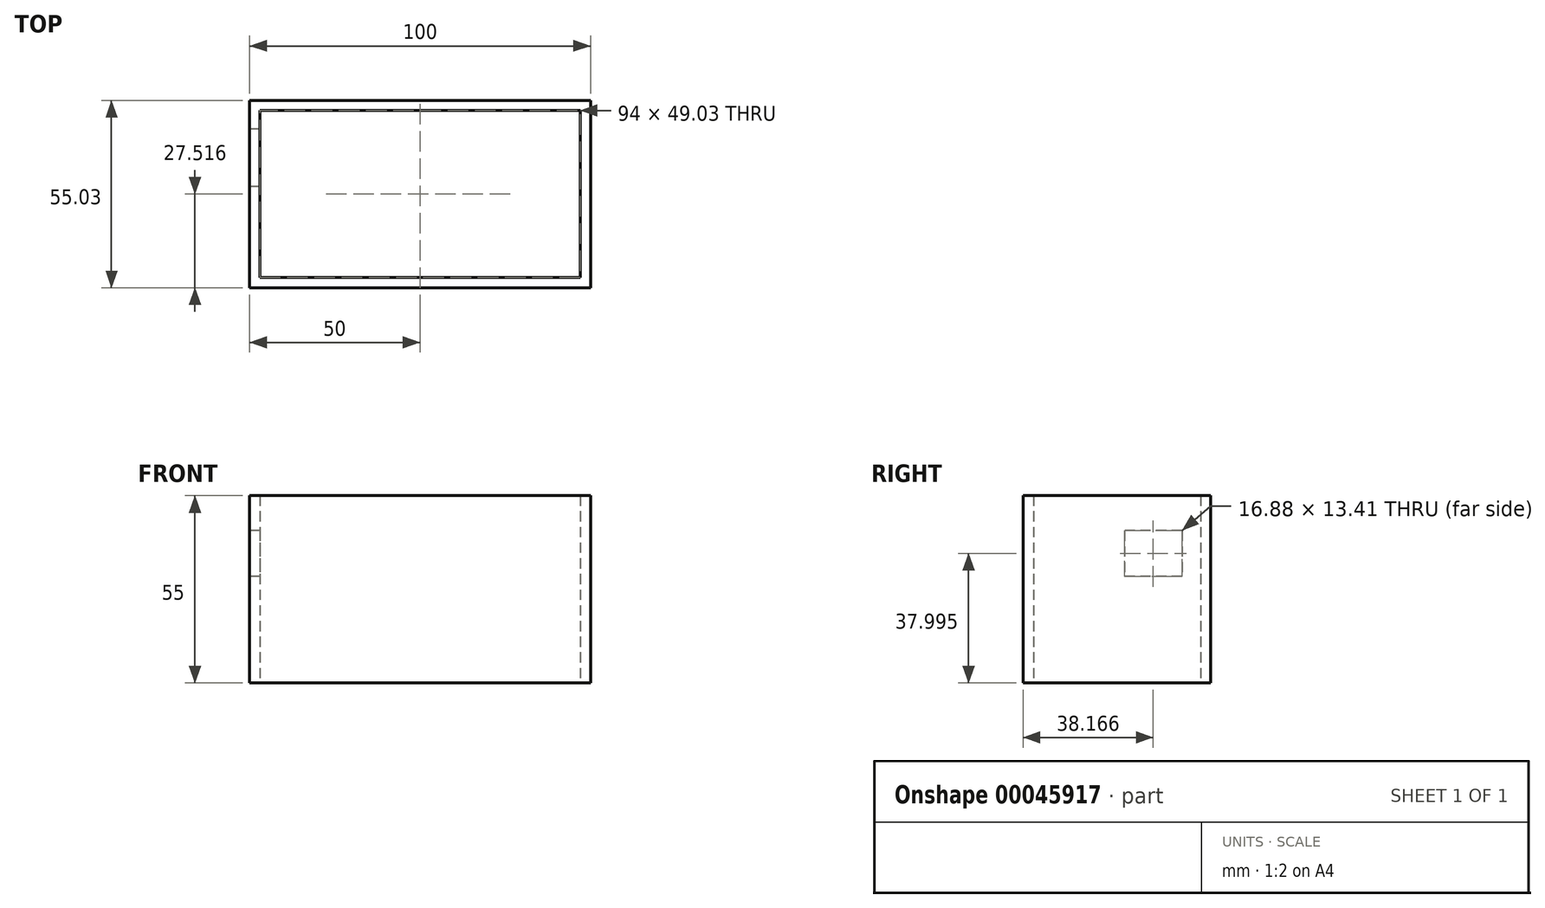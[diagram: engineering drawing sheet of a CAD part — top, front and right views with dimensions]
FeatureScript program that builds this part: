
annotation { "Feature Type Name" : "Feature", "Feature Type Description" : "" }
export const myFeature = defineFeature(function(context is Context, id is Id, definition is map)
    precondition{}
    {
        {
            var Q0;
            Q0=qCreatedBy(makeId("Top.planeOp"),FACE);
            var sketch = newSketch(context, id + "F0", { "sketchPlane" : qUnion([Q0])});
            skLineSegment(sketch, "E0.bottom", {"start": v(3, 0) * mm, "end": v(-97, 0) * mm});
            skLineSegment(sketch, "E0.top", {"start": v(3, 55.03) * mm, "end": v(-97, 55.03) * mm});
            skLineSegment(sketch, "E0.left", {"start": v(3, 0) * mm, "end": v(3, 55.03) * mm});
            skLineSegment(sketch, "E0.right", {"start": v(-97, 0) * mm, "end": v(-97, 55.03) * mm});
            skLineSegment(sketch, "E1.bottom", {"start": v(-94, 52.03) * mm, "end": v(0, 52.03) * mm});
            skLineSegment(sketch, "E1.top", {"start": v(-94, 3) * mm, "end": v(0, 3) * mm});
            skLineSegment(sketch, "E1.left", {"start": v(-94, 52.03) * mm, "end": v(-94, 3) * mm});
            skLineSegment(sketch, "E1.right", {"start": v(0, 52.03) * mm, "end": v(0, 3) * mm});
            skSolve(sketch);
        }
        {
            var Q0;
            Q0=makeQuery(id+"F0.imprint","IMPRINT",FACE,{"disambiguationData":[TD([[makeQuery(id+"F0.imprint","IMPRINT",EDGE,{"derivedFrom":sQuery(id+"F0.wireOp",EDGE,"E0.bottom")}),-1.0]])]});
            extrude(context, id + "F1", {"entities" : qUnion([Q0]), "depth" : 55 * mm});
        }
        {
            var Q0;
            Q0=makeQuery(id+"F1.opExtrude","SWEPT_FACE",FACE,{"disambiguationData":[OSD([sQuery(id+"F0.wireOp",EDGE,"E0.right")])]});
            var sketch = newSketch(context, id + "F2", { "sketchPlane" : qUnion([Q0])});
            skLineSegment(sketch, "E2.bottom", {"start": v(-46.6, 44.7) * mm, "end": v(-29.73, 44.7) * mm});
            skLineSegment(sketch, "E2.top", {"start": v(-46.6, 31.3) * mm, "end": v(-29.73, 31.3) * mm});
            skLineSegment(sketch, "E2.left", {"start": v(-46.6, 44.7) * mm, "end": v(-46.6, 31.3) * mm});
            skLineSegment(sketch, "E2.right", {"start": v(-29.73, 44.7) * mm, "end": v(-29.73, 31.3) * mm});
            skSolve(sketch);
        }
        {
            var Q0;
            Q0=makeQuery(id+"F2.imprint","IMPRINT",FACE,{"disambiguationData":[TD([[makeQuery(id+"F2.imprint","IMPRINT",EDGE,{"derivedFrom":sQuery(id+"F2.wireOp",EDGE,"E2.bottom")}),-1.0]])]});
            var Q1;
            Q1=makeQuery(id+"F1.opExtrude","SWEPT_FACE",FACE,{"disambiguationData":[OSD([sQuery(id+"F0.wireOp",EDGE,"E1.left")])]});
            extrude(context, id + "F3", {"entities" : qUnion([Q0]), "operationType" : NewBodyOperationType.REMOVE, "endBound" : BoundingType.UP_TO_SURFACE, "oppositeDirection" : true, "endBoundEntityFace" : qUnion([Q1]), "depth" : 25 * mm});
        }
    });
